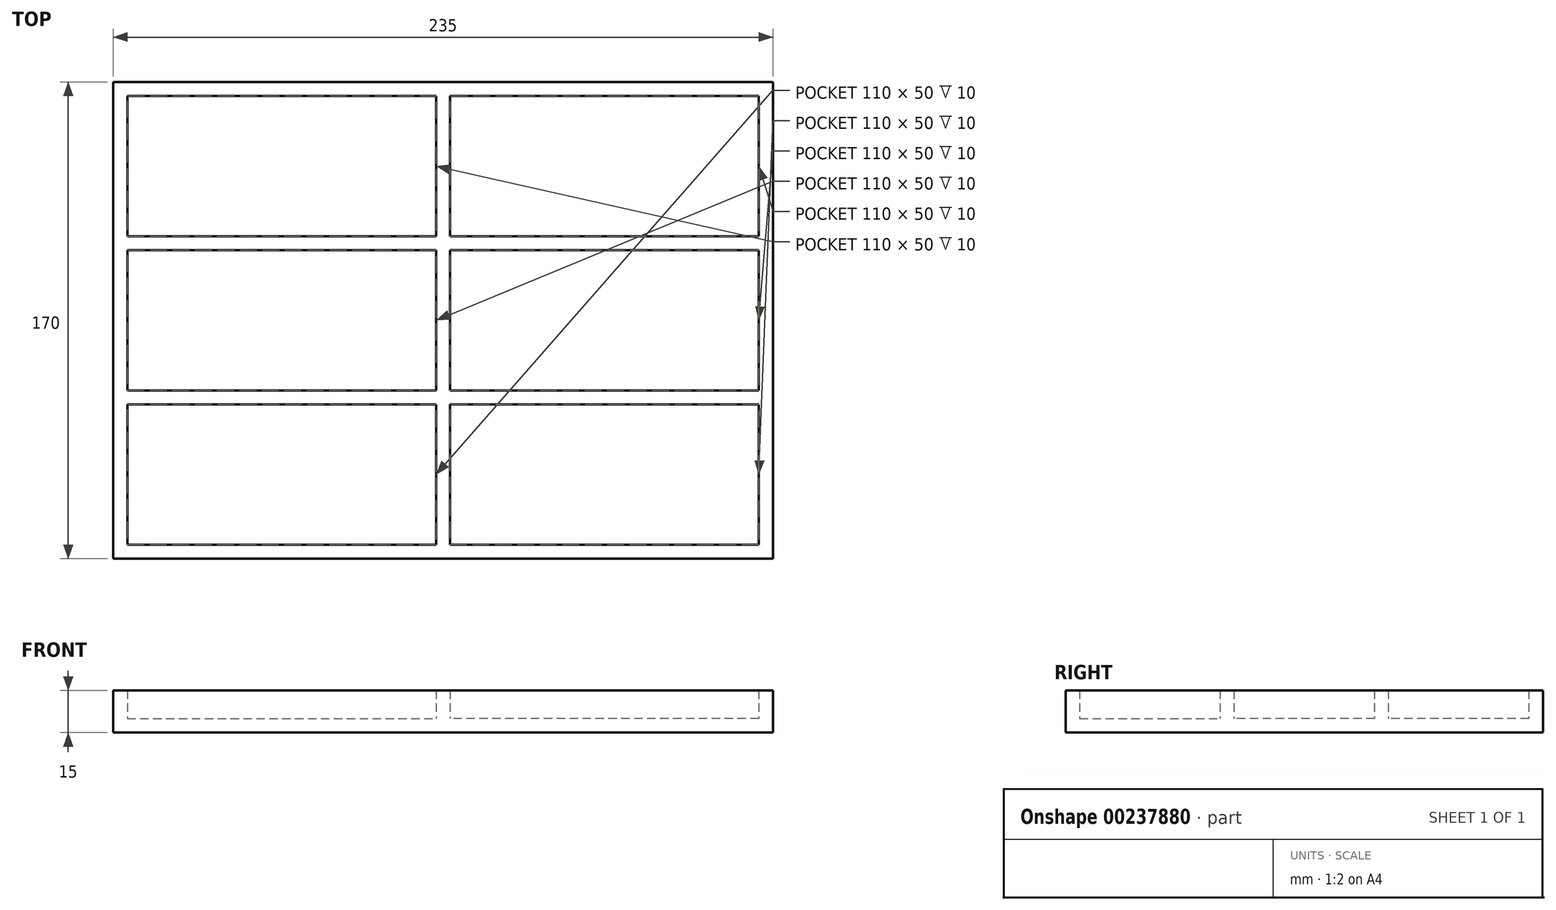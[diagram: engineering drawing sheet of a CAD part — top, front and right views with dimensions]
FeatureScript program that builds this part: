
annotation { "Feature Type Name" : "Feature", "Feature Type Description" : "" }
export const myFeature = defineFeature(function(context is Context, id is Id, definition is map)
    precondition{}
    {
        {
            var Q0;
            Q0=qCreatedBy(makeId("Top.planeOp"),FACE);
            var sketch = newSketch(context, id + "F0", { "sketchPlane" : qUnion([Q0])});
            skLineSegment(sketch, "E0.bottom", {"start": v(-117.5, 85) * mm, "end": v(117.5, 85) * mm});
            skLineSegment(sketch, "E0.top", {"start": v(-117.5, -85) * mm, "end": v(117.5, -85) * mm});
            skLineSegment(sketch, "E0.left", {"start": v(-117.5, 85) * mm, "end": v(-117.5, -85) * mm});
            skLineSegment(sketch, "E0.right", {"start": v(117.5, 85) * mm, "end": v(117.5, -85) * mm});
            skPoint(sketch, "E0.middle", {"position": v(0, 0) * mm});
            skSolve(sketch);
        }
        {
            var Q0;
            Q0=makeQuery(id+"F0.imprint","IMPRINT",FACE,{"disambiguationData":[TD([[makeQuery(id+"F0.imprint","IMPRINT",EDGE,{"derivedFrom":sQuery(id+"F0.wireOp",EDGE,"E0.bottom")}),-1.0]])]});
            extrude(context, id + "F1", {"entities" : qUnion([Q0]), "depth" : 5 * mm});
        }
        {
            var Q0;
            Q0=makeQuery(id+"F1.opExtrude","CAP_FACE",FACE,{"disambiguationData":[OSD([sQuery(id+"F0.wireOp",EDGE,"E0.bottom"),sQuery(id+"F0.wireOp",EDGE,"E0.top"),sQuery(id+"F0.wireOp",EDGE,"E0.left"),sQuery(id+"F0.wireOp",EDGE,"E0.right")])],"isStart":false});
            var sketch = newSketch(context, id + "F2", { "sketchPlane" : qUnion([Q0])});
            skLineSegment(sketch, "E1.bottom", {"start": v(-112.5, 80) * mm, "end": v(-2.5, 80) * mm});
            skLineSegment(sketch, "E1.top", {"start": v(-112.5, 30) * mm, "end": v(-2.5, 30) * mm});
            skLineSegment(sketch, "E1.left", {"start": v(-112.5, 80) * mm, "end": v(-112.5, 30) * mm});
            skLineSegment(sketch, "E1.right", {"start": v(-2.5, 80) * mm, "end": v(-2.5, 30) * mm});
            skLineSegment(sketch, "E2.MirrorCS", {"start": v(2.5, 80) * mm, "end": v(2.5, 30) * mm});
            skLineSegment(sketch, "E3.MirrorCS", {"start": v(112.5, 30) * mm, "end": v(2.5, 30) * mm});
            skLineSegment(sketch, "E4.MirrorCS", {"start": v(112.5, 80) * mm, "end": v(2.5, 80) * mm});
            skLineSegment(sketch, "E5.MirrorCS", {"start": v(112.5, 80) * mm, "end": v(112.5, 30) * mm});
            skLineSegment(sketch, "E6.MirrorCS", {"start": v(-112.5, -30) * mm, "end": v(-2.5, -30) * mm});
            skLineSegment(sketch, "E7.MirrorCS", {"start": v(-112.5, -80) * mm, "end": v(-112.5, -30) * mm});
            skLineSegment(sketch, "E8.MirrorCS", {"start": v(-112.5, -80) * mm, "end": v(-2.5, -80) * mm});
            skLineSegment(sketch, "E9.MirrorCS", {"start": v(-2.5, -80) * mm, "end": v(-2.5, -30) * mm});
            skLineSegment(sketch, "E10.MirrorCS", {"start": v(2.5, -80) * mm, "end": v(2.5, -30) * mm});
            skLineSegment(sketch, "E11.MirrorCS", {"start": v(112.5, -80) * mm, "end": v(2.5, -80) * mm});
            skLineSegment(sketch, "E12.MirrorCS", {"start": v(112.5, -30) * mm, "end": v(2.5, -30) * mm});
            skLineSegment(sketch, "E13.MirrorCS", {"start": v(112.5, -80) * mm, "end": v(112.5, -30) * mm});
            skLineSegment(sketch, "E14.bottom", {"start": v(-112.5, 25) * mm, "end": v(-2.5, 25) * mm});
            skLineSegment(sketch, "E14.top", {"start": v(-112.5, -25) * mm, "end": v(-2.5, -25) * mm});
            skLineSegment(sketch, "E14.left", {"start": v(-112.5, 25) * mm, "end": v(-112.5, -25) * mm});
            skLineSegment(sketch, "E14.right", {"start": v(-2.5, 25) * mm, "end": v(-2.5, -25) * mm});
            skLineSegment(sketch, "E15.MirrorCS", {"start": v(2.5, 25) * mm, "end": v(2.5, -25) * mm});
            skLineSegment(sketch, "E16.MirrorCS", {"start": v(112.5, 25) * mm, "end": v(2.5, 25) * mm});
            skLineSegment(sketch, "E17.MirrorCS", {"start": v(112.5, 25) * mm, "end": v(112.5, -25) * mm});
            skLineSegment(sketch, "E18.MirrorCS", {"start": v(112.5, -25) * mm, "end": v(2.5, -25) * mm});
            skSolve(sketch);
        }
        {
            var Q0;
            Q0=makeQuery(id+"F2.imprint","IMPRINT",FACE,{"disambiguationData":[TD([[makeQuery(id+"F2.imprint","IMPRINT",EDGE,{"derivedFrom":sQuery(id+"F2.wireOp",EDGE,"E1.bottom")}),1.0]])]});
            extrude(context, id + "F3", {"entities" : qUnion([Q0]), "operationType" : NewBodyOperationType.ADD, "depth" : 10 * mm});
        }
    });
